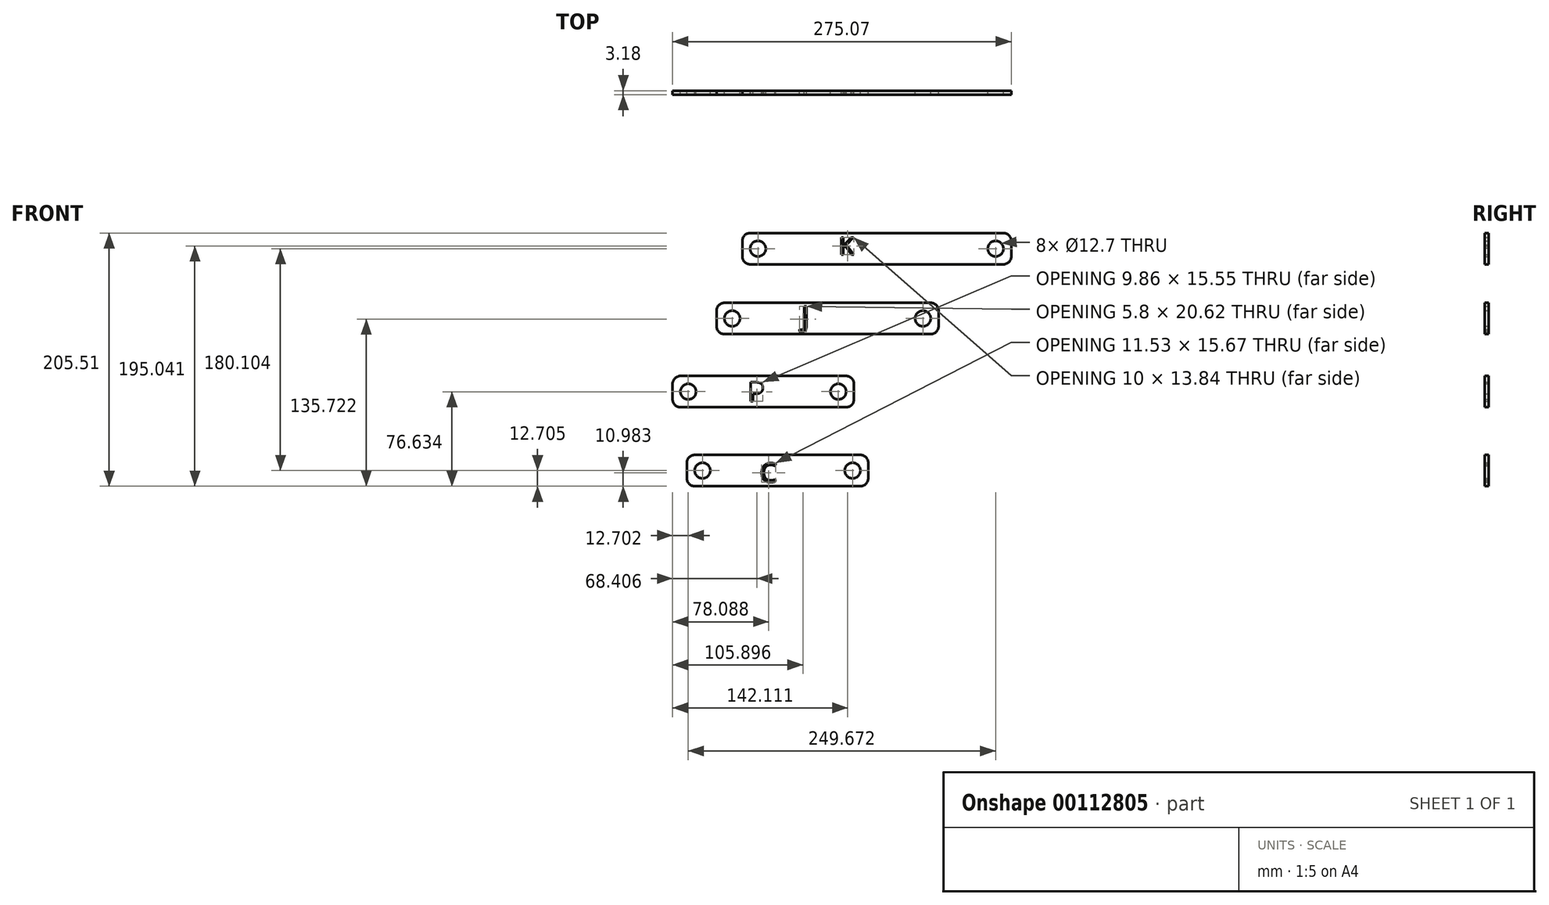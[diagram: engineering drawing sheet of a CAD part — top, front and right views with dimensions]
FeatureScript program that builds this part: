
annotation { "Feature Type Name" : "Feature", "Feature Type Description" : "" }
export const myFeature = defineFeature(function(context is Context, id is Id, definition is map)
    precondition{}
    {
        {
            var Q0;
            Q0=qCreatedBy(makeId("Front.planeOp"),FACE);
            var sketch = newSketch(context, id + "F0", { "sketchPlane" : qUnion([Q0])});
            skLineSegment(sketch, "E0", {"start": v(-144.78, -1.15) * mm, "end": v(48.26, -1.15) * mm, "construction": true});
            skLineSegment(sketch, "E1.bottom", {"start": v(-151.13, 11.55) * mm, "end": v(54.61, 11.55) * mm});
            skLineSegment(sketch, "E1.top", {"start": v(-151.13, -13.85) * mm, "end": v(54.61, -13.85) * mm});
            skLineSegment(sketch, "E1.left", {"start": v(-157.48, 5.2) * mm, "end": v(-157.48, -7.5) * mm});
            skLineSegment(sketch, "E1.right", {"start": v(60.96, 5.2) * mm, "end": v(60.96, -7.5) * mm});
            skCircle(sketch, "E2", {"center": v(-144.78, -1.15) * mm, "radius": 6.35 * mm});
            skCircle(sketch, "E3", {"center": v(48.26, -1.15) * mm, "radius": 6.35 * mm});
            skPoint(sketch, "E4.visualSharp", {"position": v(-157.48, 11.55) * mm});
            skArc(sketch, "E4.filletArc", {"start": v(-151.13, 11.55) * mm, "mid": v(-155.62, 9.69) * mm, "end": v(-157.48, 5.2) * mm});
            skPoint(sketch, "E5.visualSharp", {"position": v(-157.48, -13.85) * mm});
            skArc(sketch, "E5.filletArc", {"start": v(-157.48, -7.5) * mm, "mid": v(-155.62, -12) * mm, "end": v(-151.13, -13.85) * mm});
            skPoint(sketch, "E6.visualSharp", {"position": v(60.96, -13.85) * mm});
            skArc(sketch, "E6.filletArc", {"start": v(54.61, -13.85) * mm, "mid": v(59.1, -12) * mm, "end": v(60.96, -7.5) * mm});
            skPoint(sketch, "E7.visualSharp", {"position": v(60.96, 11.55) * mm});
            skArc(sketch, "E7.filletArc", {"start": v(60.96, 5.2) * mm, "mid": v(59.1, 9.69) * mm, "end": v(54.61, 11.55) * mm});
            skText(sketch, "E8", { "text": "K", "fontName": "OpenSans-Regular.ttf"});
            const initialGuessF0  = {"E8": [-0.0789, -0.00584, 1, 0, 0.01396]};
            skSetInitialGuess(sketch, initialGuessF0);
            skSolve(sketch);
        }
        {
            var Q0;
            Q0=makeQuery(id+"F0.imprint","IMPRINT",FACE,{"disambiguationData":[TD([[makeQuery(id+"F0.imprint","IMPRINT",EDGE,{"derivedFrom":sQuery(id+"F0.wireOp",EDGE,"E1.bottom")}),-1.0]])]});
            extrude(context, id + "F1", {"entities" : qUnion([Q0]), "depth" : 3.17 * mm});
        }
        {
            var Q0;
            Q0=qCreatedBy(makeId("Front.planeOp"),FACE);
            var sketch = newSketch(context, id + "F2", { "sketchPlane" : qUnion([Q0])});
            skLineSegment(sketch, "E9", {"start": v(-165.68, -57.76) * mm, "end": v(-10.74, -57.76) * mm, "construction": true});
            skLineSegment(sketch, "E10.bottom", {"start": v(-172.03, -45.06) * mm, "end": v(-4.39, -45.06) * mm});
            skLineSegment(sketch, "E10.top", {"start": v(-172.03, -70.46) * mm, "end": v(-4.39, -70.46) * mm});
            skLineSegment(sketch, "E10.left", {"start": v(-178.38, -51.4) * mm, "end": v(-178.38, -64.1) * mm});
            skLineSegment(sketch, "E10.right", {"start": v(1.96, -51.4) * mm, "end": v(1.96, -64.1) * mm});
            skCircle(sketch, "E11", {"center": v(-165.68, -57.76) * mm, "radius": 6.35 * mm});
            skCircle(sketch, "E12", {"center": v(-10.74, -57.76) * mm, "radius": 6.35 * mm});
            skPoint(sketch, "E13.visualSharp", {"position": v(-178.38, -45.06) * mm});
            skArc(sketch, "E13.filletArc", {"start": v(-172.03, -45.06) * mm, "mid": v(-176.52, -46.92) * mm, "end": v(-178.38, -51.4) * mm});
            skPoint(sketch, "E14.visualSharp", {"position": v(-178.38, -70.46) * mm});
            skArc(sketch, "E14.filletArc", {"start": v(-178.38, -64.1) * mm, "mid": v(-176.52, -68.6) * mm, "end": v(-172.03, -70.46) * mm});
            skPoint(sketch, "E15.visualSharp", {"position": v(1.96, -70.46) * mm});
            skArc(sketch, "E15.filletArc", {"start": v(-4.39, -70.46) * mm, "mid": v(0.1, -68.6) * mm, "end": v(1.96, -64.1) * mm});
            skPoint(sketch, "E16.visualSharp", {"position": v(1.96, -45.06) * mm});
            skArc(sketch, "E16.filletArc", {"start": v(1.96, -51.4) * mm, "mid": v(0.1, -46.92) * mm, "end": v(-4.39, -45.06) * mm});
            skText(sketch, "E17", { "text": "J", "fontName": "OpenSans-Regular.ttf"});
            const initialGuessF2  = {"E17": [-0.10933, -0.06425, 1, 0, 0.01646]};
            skSetInitialGuess(sketch, initialGuessF2);
            skSolve(sketch);
        }
        {
            var Q0;
            Q0 = qSketchRegion(id + "F2", true);
            extrude(context, id + "F3", {"entities" : qUnion([Q0]), "depth" : 3.17 * mm});
        }
        {
            var Q0;
            Q0=qCreatedBy(makeId("Front.planeOp"),FACE);
            var sketch = newSketch(context, id + "F4", { "sketchPlane" : qUnion([Q0])});
            skLineSegment(sketch, "E18", {"start": v(-201.4, -117.21) * mm, "end": v(-79.49, -117.21) * mm, "construction": true});
            skLineSegment(sketch, "E19.bottom", {"start": v(-207.76, -104.51) * mm, "end": v(-73.14, -104.51) * mm});
            skLineSegment(sketch, "E19.top", {"start": v(-207.76, -129.91) * mm, "end": v(-73.14, -129.91) * mm});
            skLineSegment(sketch, "E19.left", {"start": v(-214.1, -110.86) * mm, "end": v(-214.1, -123.56) * mm});
            skLineSegment(sketch, "E19.right", {"start": v(-66.79, -110.86) * mm, "end": v(-66.79, -123.56) * mm});
            skCircle(sketch, "E20", {"center": v(-201.4, -117.21) * mm, "radius": 6.35 * mm});
            skCircle(sketch, "E21", {"center": v(-79.49, -117.21) * mm, "radius": 6.35 * mm});
            skPoint(sketch, "E22.visualSharp", {"position": v(-214.1, -104.51) * mm});
            skArc(sketch, "E22.filletArc", {"start": v(-207.76, -104.51) * mm, "mid": v(-212.25, -106.37) * mm, "end": v(-214.1, -110.86) * mm});
            skPoint(sketch, "E23.visualSharp", {"position": v(-214.1, -129.91) * mm});
            skArc(sketch, "E23.filletArc", {"start": v(-214.1, -123.56) * mm, "mid": v(-212.25, -128.05) * mm, "end": v(-207.76, -129.91) * mm});
            skPoint(sketch, "E24.visualSharp", {"position": v(-66.79, -129.91) * mm});
            skArc(sketch, "E24.filletArc", {"start": v(-73.14, -129.91) * mm, "mid": v(-68.65, -128.05) * mm, "end": v(-66.79, -123.56) * mm});
            skPoint(sketch, "E25.visualSharp", {"position": v(-66.79, -104.51) * mm});
            skArc(sketch, "E25.filletArc", {"start": v(-66.79, -110.86) * mm, "mid": v(-68.65, -106.37) * mm, "end": v(-73.14, -104.51) * mm});
            skText(sketch, "E26", { "text": "P", "fontName": "OpenSans-Regular.ttf"});
            const initialGuessF4  = {"E26": [-0.15277, -0.1251, 1, 0, 0.01568]};
            skSetInitialGuess(sketch, initialGuessF4);
            skSolve(sketch);
        }
        {
            var Q0;
            Q0 = qSketchRegion(id + "F4", true);
            extrude(context, id + "F5", {"entities" : qUnion([Q0]), "depth" : 3.17 * mm});
        }
        {
            var Q0;
            Q0=qCreatedBy(makeId("Front.planeOp"),FACE);
            var sketch = newSketch(context, id + "F6", { "sketchPlane" : qUnion([Q0])});
            skLineSegment(sketch, "E27", {"start": v(-189.83, -181.26) * mm, "end": v(-67.91, -181.26) * mm, "construction": true});
            skLineSegment(sketch, "E28.bottom", {"start": v(-196.18, -168.56) * mm, "end": v(-61.56, -168.56) * mm});
            skLineSegment(sketch, "E28.top", {"start": v(-196.18, -193.96) * mm, "end": v(-61.56, -193.96) * mm});
            skLineSegment(sketch, "E28.left", {"start": v(-202.53, -174.9) * mm, "end": v(-202.53, -187.6) * mm});
            skLineSegment(sketch, "E28.right", {"start": v(-55.21, -174.9) * mm, "end": v(-55.21, -187.6) * mm});
            skCircle(sketch, "E29", {"center": v(-189.83, -181.26) * mm, "radius": 6.35 * mm});
            skCircle(sketch, "E30", {"center": v(-67.91, -181.26) * mm, "radius": 6.35 * mm});
            skPoint(sketch, "E31.visualSharp", {"position": v(-202.53, -168.56) * mm});
            skArc(sketch, "E31.filletArc", {"start": v(-196.18, -168.56) * mm, "mid": v(-200.67, -170.42) * mm, "end": v(-202.53, -174.9) * mm});
            skPoint(sketch, "E32.visualSharp", {"position": v(-202.53, -193.96) * mm});
            skArc(sketch, "E32.filletArc", {"start": v(-202.53, -187.6) * mm, "mid": v(-200.67, -192.1) * mm, "end": v(-196.18, -193.96) * mm});
            skPoint(sketch, "E33.visualSharp", {"position": v(-55.21, -193.96) * mm});
            skArc(sketch, "E33.filletArc", {"start": v(-61.56, -193.96) * mm, "mid": v(-57.07, -192.1) * mm, "end": v(-55.21, -187.6) * mm});
            skPoint(sketch, "E34.visualSharp", {"position": v(-55.21, -168.56) * mm});
            skArc(sketch, "E34.filletArc", {"start": v(-55.21, -174.9) * mm, "mid": v(-57.07, -170.42) * mm, "end": v(-61.56, -168.56) * mm});
            skText(sketch, "E35", { "text": "C", "fontName": "OpenSans-Regular.ttf"});
            skPoint(sketch, "E35.secondSnap0", {"position": v(-128.87, -181.26) * mm});
            const initialGuessF6  = {"E35": [-0.14309, -0.1906, 1, 0, 0.01537]};
            skSetInitialGuess(sketch, initialGuessF6);
            skSolve(sketch);
        }
        {
            var Q0;
            Q0 = qSketchRegion(id + "F6", true);
            extrude(context, id + "F7", {"entities" : qUnion([Q0]), "depth" : 3.17 * mm});
        }
    });
